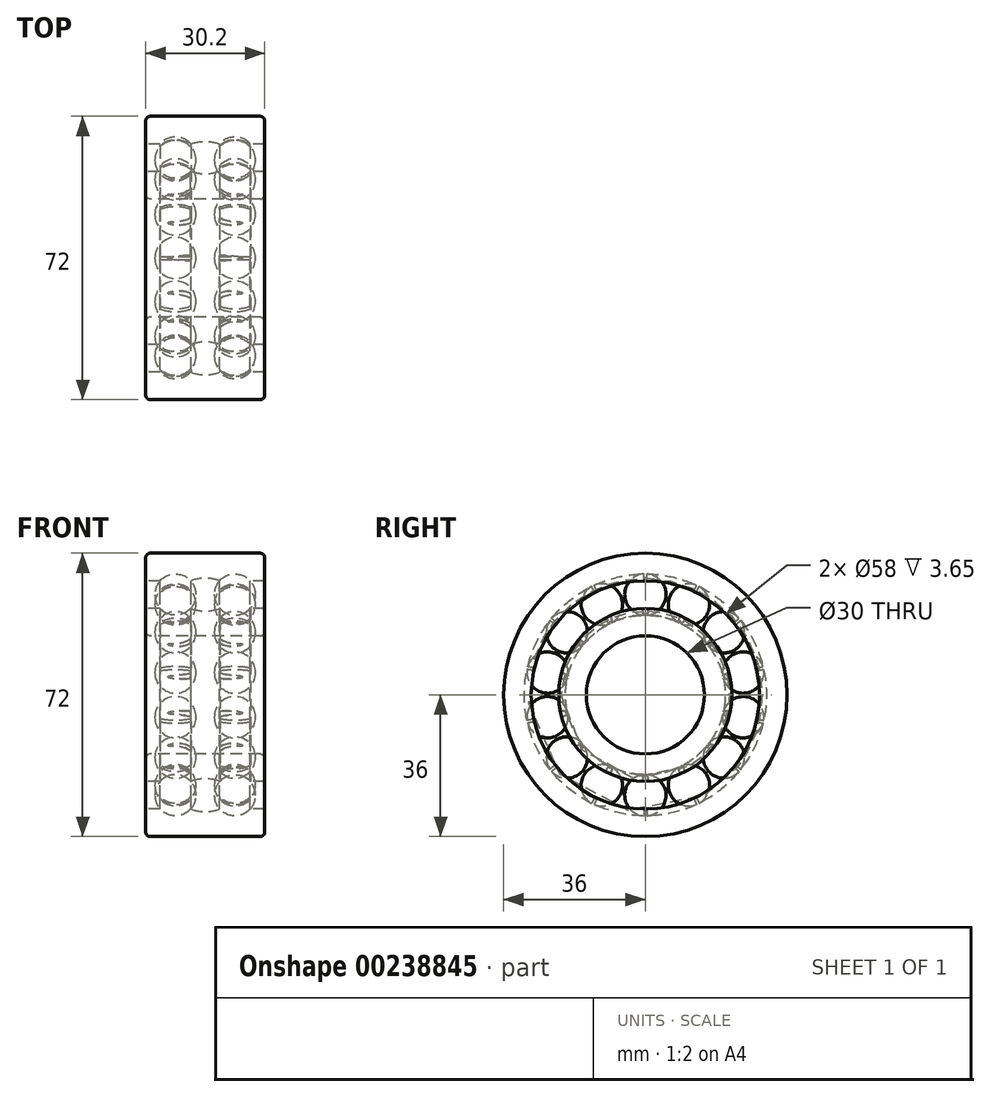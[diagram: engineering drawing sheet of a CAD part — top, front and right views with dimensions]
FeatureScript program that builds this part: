
annotation { "Feature Type Name" : "Feature", "Feature Type Description" : "" }
export const myFeature = defineFeature(function(context is Context, id is Id, definition is map)
    precondition{}
    {
        {
            var Q0;
            Q0=qCreatedBy(makeId("Front.planeOp"),FACE);
            var sketch = newSketch(context, id + "F0", { "sketchPlane" : qUnion([Q0])});
            skLineSegment(sketch, "E0", {"start": v(0, 0) * mm, "end": v(30.2, 0) * mm, "construction": true});
            skLineSegment(sketch, "E1", {"start": v(0, 22) * mm, "end": v(0, 15) * mm});
            skLineSegment(sketch, "E2", {"start": v(0, 15) * mm, "end": v(30.2, 15) * mm});
            skLineSegment(sketch, "E3", {"start": v(30.2, 15) * mm, "end": v(30.2, 22) * mm});
            skLineSegment(sketch, "E4", {"start": v(0, 22) * mm, "end": v(3.61, 22) * mm});
            skLineSegment(sketch, "E5", {"start": v(30.2, 22) * mm, "end": v(26.59, 22) * mm});
            skArc(sketch, "E6", {"start": v(3.61, 22) * mm, "mid": v(7.5, 20.27) * mm, "end": v(11.39, 22) * mm});
            skArc(sketch, "E7", {"start": v(11.39, 22) * mm, "mid": v(15.1, 21.32) * mm, "end": v(18.81, 22) * mm});
            skArc(sketch, "E8", {"start": v(18.81, 22) * mm, "mid": v(22.7, 20.27) * mm, "end": v(26.59, 22) * mm});
            skLineSegment(sketch, "E9", {"start": v(-0.17, 25.5) * mm, "end": v(34.16, 25.5) * mm, "construction": true});
            skSolve(sketch);
        }
        {
            var Q0;
            Q0=makeQuery(id+"F0.imprint","IMPRINT",FACE,{"disambiguationData":[TD([[makeQuery(id+"F0.imprint","IMPRINT",EDGE,{"derivedFrom":sQuery(id+"F0.wireOp",EDGE,"E1")}),1.0]])]});
            var Q1;
            Q1=sQuery(id+"F0.wireOp",EDGE,"E0");
            revolve(context, id + "F1", {"entities" : qUnion([Q0]), "axis" : qUnion([Q1]), "revolveType" : RevolveType.FULL});
        }
        {
            var Q0;
            Q0=qCreatedBy(makeId("Front.planeOp"),FACE);
            var sketch = newSketch(context, id + "F2", { "sketchPlane" : qUnion([Q0])});
            skLineSegment(sketch, "E10", {"start": v(0, 25.5) * mm, "end": v(40.29, 25.5) * mm, "construction": true});
            skArc(sketch, "E11", {"start": v(2.3, 25.5) * mm, "mid": v(7.55, 20.25) * mm, "end": v(12.8, 25.5) * mm, "construction": true});
            skArc(sketch, "E12", {"start": v(17.4, 25.5) * mm, "mid": v(22.65, 20.25) * mm, "end": v(27.9, 25.5) * mm, "construction": true});
            skLineSegment(sketch, "E13", {"start": v(0, 0) * mm, "end": v(30.2, 0) * mm, "construction": true});
            skPoint(sketch, "E14", {"position": v(15.1, 0) * mm});
            skArc(sketch, "E15", {"start": v(2.3, 25.5) * mm, "mid": v(7.55, 20.25) * mm, "end": v(12.8, 25.5) * mm});
            skArc(sketch, "E16", {"start": v(17.4, 25.5) * mm, "mid": v(22.65, 20.25) * mm, "end": v(27.9, 25.5) * mm});
            skLineSegment(sketch, "E17", {"start": v(2.3, 25.5) * mm, "end": v(12.8, 25.5) * mm});
            skLineSegment(sketch, "E18", {"start": v(17.4, 25.5) * mm, "end": v(27.9, 25.5) * mm});
            skSolve(sketch);
        }
        {
            var Q0;
            Q0=makeQuery(id+"F2.imprint","IMPRINT",FACE,{"disambiguationData":[TD([[makeQuery(id+"F2.imprint","IMPRINT",EDGE,{"derivedFrom":sQuery(id+"F2.wireOp",EDGE,"E15")}),1.0]])]});
            var Q1;
            Q1=makeQuery(id+"F2.imprint","IMPRINT",FACE,{"disambiguationData":[TD([[makeQuery(id+"F2.imprint","IMPRINT",EDGE,{"derivedFrom":sQuery(id+"F2.wireOp",EDGE,"E16")}),1.0]])]});
            var Q2;
            Q2=sQuery(id+"F2.wireOp",EDGE,"E10");
            revolve(context, id + "F3", {"operationType" : NewBodyOperationType.ADD, "entities" : qUnion([Q0, Q1]), "axis" : qUnion([Q2]), "revolveType" : RevolveType.FULL});
        }
        {
            var Q0;
            Q0=qCreatedBy(makeId("Front.planeOp"),FACE);
            var sketch = newSketch(context, id + "F4", { "sketchPlane" : qUnion([Q0])});
            skLineSegment(sketch, "E19", {"start": v(0, 36) * mm, "end": v(30.2, 36) * mm});
            skLineSegment(sketch, "E20", {"start": v(0, 36) * mm, "end": v(0, 29) * mm});
            skLineSegment(sketch, "E21", {"start": v(0, 29) * mm, "end": v(3.65, 29) * mm});
            skLineSegment(sketch, "E22", {"start": v(30.2, 36) * mm, "end": v(30.2, 29) * mm});
            skPoint(sketch, "E22.endSnap0", {"position": v(1.83, 29) * mm});
            skLineSegment(sketch, "E23", {"start": v(30.2, 29) * mm, "end": v(26.55, 29) * mm});
            skArc(sketch, "E24", {"start": v(11.45, 29) * mm, "mid": v(7.55, 30.74) * mm, "end": v(3.65, 29) * mm});
            skArc(sketch, "E25", {"start": v(18.75, 29) * mm, "mid": v(15.1, 29.66) * mm, "end": v(11.45, 29) * mm});
            skArc(sketch, "E26", {"start": v(26.55, 29) * mm, "mid": v(22.65, 30.74) * mm, "end": v(18.75, 29) * mm});
            skLineSegment(sketch, "E27", {"start": v(1, 25.5) * mm, "end": v(29.76, 25.5) * mm, "construction": true});
            skLineSegment(sketch, "E28", {"start": v(0, 0) * mm, "end": v(31.7, 0) * mm, "construction": true});
            skSolve(sketch);
        }
        {
            var Q0;
            Q0=makeQuery(id+"F4.imprint","IMPRINT",FACE,{"disambiguationData":[TD([[makeQuery(id+"F4.imprint","IMPRINT",EDGE,{"derivedFrom":sQuery(id+"F4.wireOp",EDGE,"E19")}),-1.0]])]});
            var Q1;
            Q1=sQuery(id+"F4.wireOp",EDGE,"E28");
            revolve(context, id + "F5", {"operationType" : NewBodyOperationType.ADD, "entities" : qUnion([Q0]), "axis" : qUnion([Q1]), "revolveType" : RevolveType.FULL});
        }
        {
            var Q0;
            Q0=makeQuery(id+"F3.opRevolve","SWEPT_FACE",FACE,{"disambiguationData":[OSD([sQuery(id+"F2.wireOp",EDGE,"E16")])]});
            var Q1;
            Q1=makeQuery(id+"F3.opRevolve","SWEPT_FACE",FACE,{"disambiguationData":[OSD([sQuery(id+"F2.wireOp",EDGE,"E15")])]});
            var Q2;
            Q2=makeQuery(id+"F1.opRevolve","SWEPT_EDGE",EDGE,{"disambiguationData":[OSD([sQuery(id+"F0.wireOp",EDGE,"E1"),sQuery(id+"F0.wireOp",EDGE,"E4")])]});
            circularPattern(context, id + "F6", {"patternType" : PatternType.FACE, "faces" : qUnion([Q0, Q1]), "axis" : qUnion([Q2]), "angle" : 360 * degree, "instanceCount" : 14, "equalSpace" : true});
        }
        {
            var Q0;
            Q0=makeQuery(id+"F5.opRevolve","SWEPT_EDGE",EDGE,{"disambiguationData":[OSD([sQuery(id+"F4.wireOp",EDGE,"E19"),sQuery(id+"F4.wireOp",EDGE,"E20")])]});
            var Q1;
            Q1=makeQuery(id+"F1.opRevolve","SWEPT_EDGE",EDGE,{"disambiguationData":[OSD([sQuery(id+"F0.wireOp",EDGE,"E1"),sQuery(id+"F0.wireOp",EDGE,"E2")])]});
            var Q2;
            Q2=makeQuery(id+"F5.opRevolve","SWEPT_EDGE",EDGE,{"disambiguationData":[OSD([sQuery(id+"F4.wireOp",EDGE,"E19"),sQuery(id+"F4.wireOp",EDGE,"E22")])]});
            var Q3;
            Q3=makeQuery(id+"F1.opRevolve","SWEPT_EDGE",EDGE,{"disambiguationData":[OSD([sQuery(id+"F0.wireOp",EDGE,"E2"),sQuery(id+"F0.wireOp",EDGE,"E3")])]});
            fillet(context, id + "F7", {"entities" : qUnion([Q0, Q1, Q2, Q3]), "radius" : 1.1 * mm, "tangentPropagation" : true, "allowEdgeOverflow" : false});
        }
    });
